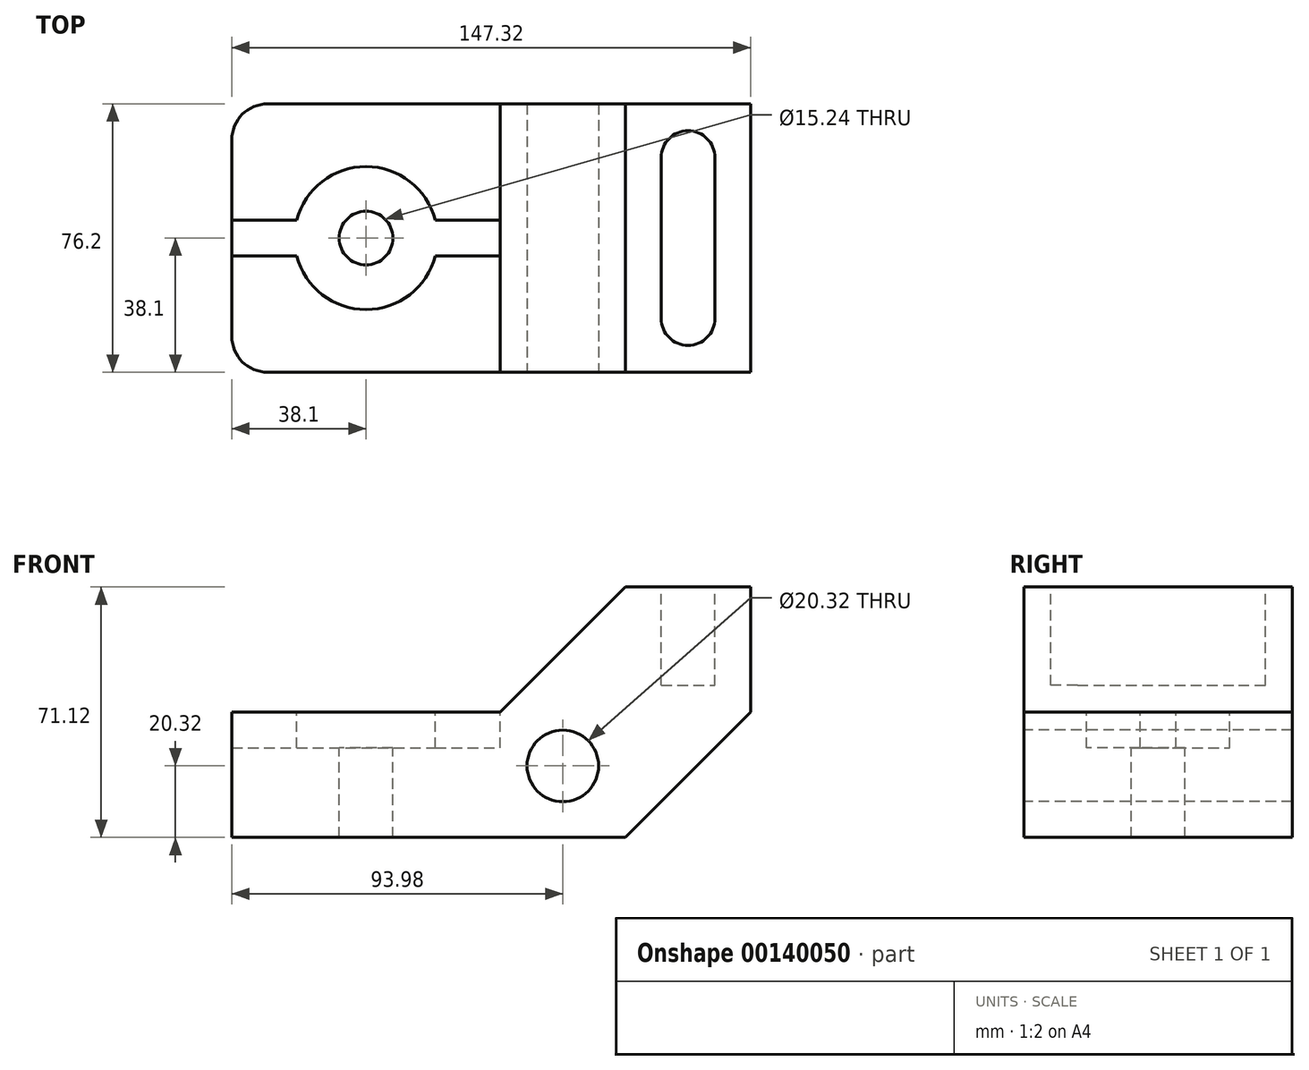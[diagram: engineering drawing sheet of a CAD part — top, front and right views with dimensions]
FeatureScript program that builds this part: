
annotation { "Feature Type Name" : "Feature", "Feature Type Description" : "" }
export const myFeature = defineFeature(function(context is Context, id is Id, definition is map)
    precondition{}
    {
        {
            var Q0;
            Q0=qCreatedBy(makeId("Front.planeOp"),FACE);
            var sketch = newSketch(context, id + "F0", { "sketchPlane" : qUnion([Q0])});
            skLineSegment(sketch, "E0", {"start": v(0, 0) * mm, "end": v(111.76, 0) * mm});
            skLineSegment(sketch, "E1", {"start": v(147.32, 35.56) * mm, "end": v(111.76, 0) * mm});
            skLineSegment(sketch, "E2", {"start": v(147.32, 35.56) * mm, "end": v(147.32, 71.12) * mm});
            skLineSegment(sketch, "E3", {"start": v(147.32, 71.12) * mm, "end": v(111.76, 71.12) * mm});
            skLineSegment(sketch, "E4", {"start": v(0, 0) * mm, "end": v(0, 35.56) * mm});
            skLineSegment(sketch, "E5", {"start": v(0, 35.56) * mm, "end": v(76.2, 35.56) * mm});
            skLineSegment(sketch, "E6", {"start": v(76.2, 35.56) * mm, "end": v(111.76, 71.12) * mm});
            skSolve(sketch);
        }
        {
            var Q0;
            Q0=makeQuery(id+"F0.imprint","IMPRINT",FACE,{"disambiguationData":[TD([[makeQuery(id+"F0.imprint","IMPRINT",EDGE,{"derivedFrom":sQuery(id+"F0.wireOp",EDGE,"E0")}),1.0]])]});
            extrude(context, id + "F1", {"entities" : qUnion([Q0]), "endBound" : BoundingType.SYMMETRIC, "depth" : 76.2 * mm});
        }
        {
            var Q0;
            Q0=makeQuery(id+"F1.opExtrude","CAP_EDGE",EDGE,{"disambiguationData":[OSD([sQuery(id+"F0.wireOp",EDGE,"E4")])],"isStart":false});
            var Q1;
            Q1=makeQuery(id+"F1.opExtrude","CAP_EDGE",EDGE,{"disambiguationData":[OSD([sQuery(id+"F0.wireOp",EDGE,"E4")])],"isStart":true});
            fillet(context, id + "F2", {"entities" : qUnion([Q0, Q1]), "radius" : 10.16 * mm, "tangentPropagation" : true, "allowEdgeOverflow" : false});
        }
        {
            var Q0;
            Q0=makeQuery(id+"F1.opExtrude","CAP_FACE",FACE,{"disambiguationData":[OSD([sQuery(id+"F0.wireOp",EDGE,"E0"),sQuery(id+"F0.wireOp",EDGE,"E1"),sQuery(id+"F0.wireOp",EDGE,"E2"),sQuery(id+"F0.wireOp",EDGE,"E3"),sQuery(id+"F0.wireOp",EDGE,"E4"),sQuery(id+"F0.wireOp",EDGE,"E5"),sQuery(id+"F0.wireOp",EDGE,"E6")])],"isStart":false});
            var sketch = newSketch(context, id + "F3", { "sketchPlane" : qUnion([Q0])});
            skLineSegment(sketch, "E7.0.0", {"start": v(10.16, 0) * mm, "end": v(0, 0) * mm});
            skLineSegment(sketch, "E7.0.1", {"start": v(10.16, 35.56) * mm, "end": v(10.16, 0) * mm});
            skLineSegment(sketch, "E7.0.2", {"start": v(10.16, 35.56) * mm, "end": v(0, 35.56) * mm});
            skLineSegment(sketch, "E7.0.3", {"start": v(0, 35.56) * mm, "end": v(0, 0) * mm});
            skCircle(sketch, "E8", {"center": v(93.98, 20.32) * mm, "radius": 10.16 * mm});
            skSolve(sketch);
        }
        {
            var Q0;
            Q0=makeQuery(id+"F3.imprint","IMPRINT",FACE,{"disambiguationData":[TD([[makeQuery(id+"F3.imprint","IMPRINT",EDGE,{"derivedFrom":sQuery(id+"F3.wireOp",EDGE,"E8")}),1.0]])]});
            extrude(context, id + "F4", {"entities" : qUnion([Q0]), "operationType" : NewBodyOperationType.REMOVE, "endBound" : BoundingType.THROUGH_ALL, "oppositeDirection" : true, "depth" : 25.4 * mm});
        }
        {
            var Q0;
            Q0=makeQuery(id+"F1.opExtrude","SWEPT_FACE",FACE,{"disambiguationData":[OSD([sQuery(id+"F0.wireOp",EDGE,"E3")])]});
            var sketch = newSketch(context, id + "F5", { "sketchPlane" : qUnion([Q0])});
            skArc(sketch, "E9", {"start": v(137.16, 22.86) * mm, "mid": v(129.54, 30.48) * mm, "end": v(121.92, 22.86) * mm});
            skPoint(sketch, "E9.centerSnap0", {"position": v(129.54, 38.1) * mm});
            skArc(sketch, "E10", {"start": v(121.92, -22.86) * mm, "mid": v(129.54, -30.48) * mm, "end": v(137.16, -22.86) * mm});
            skLineSegment(sketch, "E11", {"start": v(137.16, -22.86) * mm, "end": v(137.16, 22.86) * mm});
            skLineSegment(sketch, "E12", {"start": v(121.92, 22.86) * mm, "end": v(121.92, -22.86) * mm});
            skSolve(sketch);
        }
        {
            var Q0;
            Q0=makeQuery(id+"F5.imprint","IMPRINT",FACE,{"disambiguationData":[TD([[makeQuery(id+"F5.imprint","IMPRINT",EDGE,{"derivedFrom":sQuery(id+"F5.wireOp",EDGE,"E9")}),1.0]])]});
            extrude(context, id + "F6", {"entities" : qUnion([Q0]), "operationType" : NewBodyOperationType.REMOVE, "oppositeDirection" : true, "depth" : 27.94 * mm});
        }
        {
            var Q0;
            Q0=makeQuery(id+"F1.opExtrude","SWEPT_FACE",FACE,{"disambiguationData":[OSD([sQuery(id+"F0.wireOp",EDGE,"E5")])]});
            var sketch = newSketch(context, id + "F7", { "sketchPlane" : qUnion([Q0])});
            skPoint(sketch, "E13", {"position": v(38.1, 0) * mm});
            skSolve(sketch);
        }
        {
            var Q0;
            Q0=sQuery(id+"F7.wireOp",VERTEX,"E13");
            var Q1;
            Q1=makeQuery(id+"F1.opExtrude","SWEPT_BODY",BODY,{"disambiguationData":[OSD([sQuery(id+"F0.wireOp",EDGE,"E0"),sQuery(id+"F0.wireOp",EDGE,"E1"),sQuery(id+"F0.wireOp",EDGE,"E2"),sQuery(id+"F0.wireOp",EDGE,"E3"),sQuery(id+"F0.wireOp",EDGE,"E4"),sQuery(id+"F0.wireOp",EDGE,"E5"),sQuery(id+"F0.wireOp",EDGE,"E6")])]});
            hole(context, id + "F8", {"style" : HoleStyle.C_BORE, "endStyle" : HoleEndStyle.THROUGH, "holeDiameter" : 15.24 * mm, "cBoreDiameter" : 40.64 * mm, "cBoreDepth" : 10.16 * mm, "locations" : qUnion([Q0]), "scope" : qUnion([Q1]), "isTappedThrough" : true});
        }
        {
            var Q0;
            Q0=makeQuery(id+"F1.opExtrude","SWEPT_FACE",FACE,{"disambiguationData":[OSD([sQuery(id+"F0.wireOp",EDGE,"E5")])]});
            var sketch = newSketch(context, id + "F9", { "sketchPlane" : qUnion([Q0])});
            skLineSegment(sketch, "E14", {"start": v(0, 0) * mm, "end": v(76.2, 0) * mm, "construction": true});
            skLineSegment(sketch, "E15", {"start": v(0, 5.08) * mm, "end": v(18.43, 5.08) * mm});
            skLineSegment(sketch, "E16", {"start": v(0, -5.08) * mm, "end": v(18.43, -5.08) * mm});
            skLineSegment(sketch, "E17", {"start": v(57.77, 5.08) * mm, "end": v(76.2, 5.08) * mm});
            skLineSegment(sketch, "E18", {"start": v(57.77, -5.08) * mm, "end": v(76.2, -5.08) * mm});
            skSolve(sketch);
        }
        {
            var Q0;
            {var subQ0=sQuery(id+"F9.wireOp",EDGE,"E15");Q0=makeQuery(id+"F9.imprint","IMPRINT",FACE,{"disambiguationData":[TD([[makeQuery(id+"F9.imprint","IMPRINT",EDGE,{"derivedFrom":subQ0}),-1.0]])]});}
            var Q1;
            {var subQ0=sQuery(id+"F9.wireOp",EDGE,"E17");Q1=makeQuery(id+"F9.imprint","IMPRINT",FACE,{"disambiguationData":[TD([[makeQuery(id+"F9.imprint","IMPRINT",EDGE,{"derivedFrom":subQ0}),-1.0]])]});}
            extrude(context, id + "F10", {"entities" : qUnion([Q0, Q1]), "operationType" : NewBodyOperationType.REMOVE, "oppositeDirection" : true, "depth" : 10.16 * mm});
        }
    });
